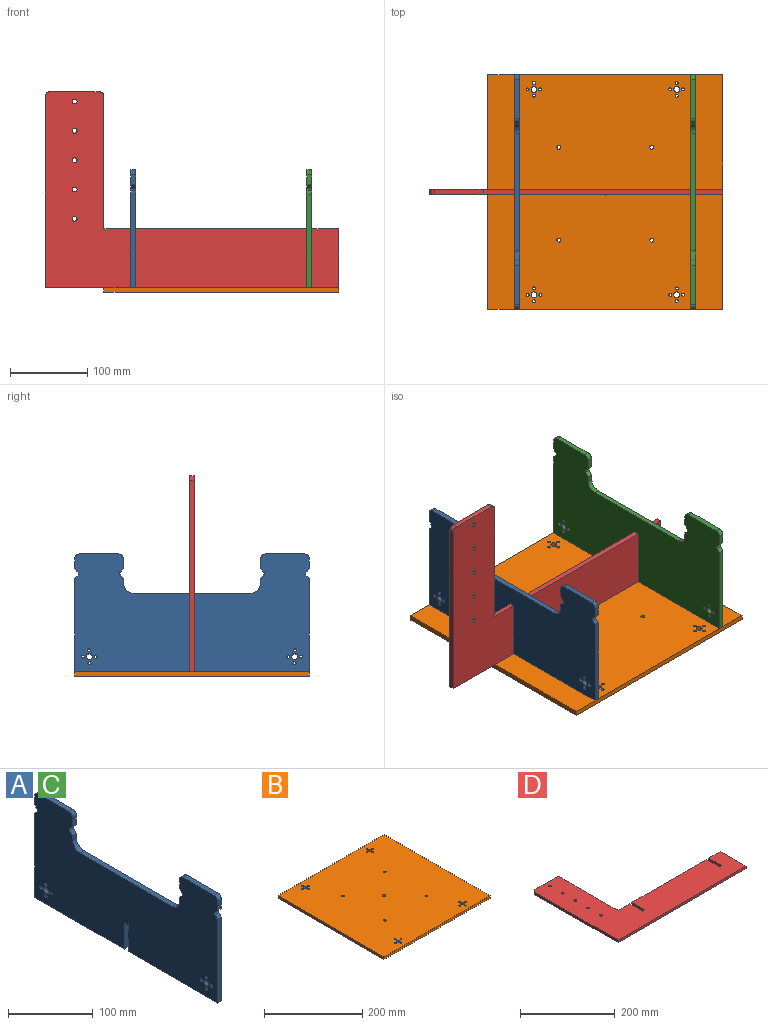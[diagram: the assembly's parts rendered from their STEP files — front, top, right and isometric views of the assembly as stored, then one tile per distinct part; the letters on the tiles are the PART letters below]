
ASSEMBLY  parts=4 mates=7
PART A: 46 faces, bbox 6.4x304.8x152.4 mm
  f0: plane 304.8x152.4mm, normal (1,0,0), area 36873.8mm2, adj f2,f3,f4,f5,f6,f7,f8,f9
  f1: plane 304.8x152.4mm, normal (-1,0,0), area 36873.8mm2, adj f2,f3,f4,f5,f6,f7,f8,f9
  f2: plane 149.23x6.35mm, normal (0,0,-1), area 947.6mm2, adj f0,f1,f4,f35
  f3: plane 149.23x6.35mm, normal (0,0,-1), area 947.6mm2, adj f0,f1,f32,f34
  f4: plane 120.65x6.35mm, normal (0,1,0), area 766.1mm2, adj f0,f1,f2,f5
  f5: plane 6.35x4.55mm, normal (0,0.71,0.71), area 40.9mm2, adj f0,f1,f4,f6
  f6: cylinder r=2.54mm len=6.35mm, axis (-1,0,0), area 25.3mm2, adj f0,f1,f5,f7
  f7: plane 6.35x4.55mm, normal (0,0.71,-0.71), area 40.9mm2, adj f0,f1,f6,f8
  f8: plane 12.7x6.35mm, normal (0,1,0), area 80.6mm2, adj f0,f1,f7,f9
  f9: cylinder r=6.35mm len=6.35mm, axis (-1,0,0), area 63.3mm2, adj f0,f1,f8,f10
  f10: plane 50.8x6.35mm, normal (0,0,1), area 322.6mm2, adj f0,f1,f9,f11
  f11: cylinder r=6.35mm len=6.35mm, axis (-1,0,0), area 63.3mm2, adj f0,f1,f10,f12
  f12: plane 12.7x6.35mm, normal (0,-1,0), area 80.6mm2, adj f0,f1,f11,f13
  f13: plane 6.35x4.55mm, normal (0,-0.71,-0.71), area 40.9mm2, adj f0,f1,f12,f14
  f14: cylinder r=2.54mm len=6.35mm, axis (-1,0,0), area 25.3mm2, adj f0,f1,f13,f15
  f15: plane 6.35x4.55mm, normal (0,-0.71,0.71), area 40.9mm2, adj f0,f1,f14,f16
  f16: plane 6.35x6.35mm, normal (0,-1,0), area 40.3mm2, adj f0,f1,f15,f17
  f17: cylinder r=12.7mm len=12.7mm, axis (-1,0,0), area 126.7mm2, adj f0,f1,f16,f18
  f18: plane 152.4x6.35mm, normal (0,0,1), area 967.7mm2, adj f0,f1,f17,f19
  f19: cylinder r=12.7mm len=12.7mm, axis (-1,0,0), area 126.7mm2, adj f0,f1,f18,f20
  f20: plane 6.35x6.35mm, normal (0,1,0), area 40.3mm2, adj f0,f1,f19,f21
  f21: plane 6.35x4.55mm, normal (0,0.71,0.71), area 40.9mm2, adj f0,f1,f20,f22
  f22: cylinder r=2.54mm len=6.35mm, axis (-1,0,0), area 25.3mm2, adj f0,f1,f21,f23
  f23: plane 6.35x4.55mm, normal (0,0.71,-0.71), area 40.9mm2, adj f0,f1,f22,f24
  f24: plane 12.7x6.35mm, normal (0,1,0), area 80.6mm2, adj f0,f1,f23,f25
  f25: cylinder r=6.35mm len=6.35mm, axis (-1,0,0), area 63.3mm2, adj f0,f1,f24,f26
  f26: plane 50.8x6.35mm, normal (0,0,1), area 322.6mm2, adj f0,f1,f25,f27
  f27: cylinder r=6.35mm len=6.35mm, axis (-1,0,0), area 63.3mm2, adj f0,f1,f26,f28
  f28: plane 12.7x6.35mm, normal (0,-1,0), area 80.6mm2, adj f0,f1,f27,f29
  f29: plane 6.35x4.55mm, normal (0,-0.71,-0.71), area 40.9mm2, adj f0,f1,f28,f30
  f30: cylinder r=2.54mm len=6.35mm, axis (-1,0,0), area 25.3mm2, adj f0,f1,f29,f31
  f31: plane 6.35x4.55mm, normal (0,-0.71,0.71), area 40.9mm2, adj f0,f1,f30,f32
  f32: plane 120.65x6.35mm, normal (0,-1,0), area 766.1mm2, adj f0,f1,f3,f31
  f33: plane 6.35x6.35mm, normal (0,0,-1), area 40.3mm2, adj f0,f1,f34,f35
  f34: plane 38.1x6.35mm, normal (0,1,0), area 241.9mm2, adj f0,f1,f3,f33
  f35: plane 38.1x6.35mm, normal (0,-1,0), area 241.9mm2, adj f0,f1,f2,f33
  f36: cylinder r=3.81mm len=7.62mm, axis (1,0,0), area 152mm2, adj f0,f1
  f37: cylinder r=1.91mm len=6.35mm, axis (1,0,0), area 76mm2, adj f0,f1
  f38: cylinder r=3.81mm len=7.62mm, axis (1,0,0), area 152mm2, adj f0,f1
  f39: cylinder r=1.91mm len=6.35mm, axis (1,0,0), area 76mm2, adj f0,f1
  f40: cylinder r=1.91mm len=6.35mm, axis (1,0,0), area 76mm2, adj f0,f1
  f41: cylinder r=1.91mm len=6.35mm, axis (1,0,0), area 76mm2, adj f0,f1
  f42: cylinder r=1.91mm len=6.35mm, axis (1,0,0), area 76mm2, adj f0,f1
  f43: cylinder r=1.91mm len=6.35mm, axis (1,0,0), area 76mm2, adj f0,f1
  f44: cylinder r=1.91mm len=6.35mm, axis (1,0,0), area 76mm2, adj f0,f1
  f45: cylinder r=1.91mm len=6.35mm, axis (1,0,0), area 76mm2, adj f0,f1
PART B: 31 faces, bbox 304.8x304.8x6.4 mm
  f0: plane 304.8x6.35mm, normal (-1,0,0), area 1935.5mm2, adj f1,f28,f29,f30
  f1: plane 304.8x6.35mm, normal (0,-1,0), area 1935.5mm2, adj f0,f2,f29,f30
  f2: plane 304.8x6.35mm, normal (1,0,0), area 1935.5mm2, adj f1,f28,f29,f30
  f3: cylinder r=3.81mm len=7.62mm, axis (0,0,-1), area 152mm2, adj f29,f30
  f4: cylinder r=3.81mm len=7.62mm, axis (0,0,-1), area 152mm2, adj f29,f30
  f5: cylinder r=3.81mm len=7.62mm, axis (0,0,-1), area 152mm2, adj f29,f30
  f6: cylinder r=3.81mm len=7.62mm, axis (0,0,-1), area 152mm2, adj f29,f30
  f7: cylinder r=3.81mm len=7.62mm, axis (0,0,-1), area 152mm2, adj f29,f30
  f8: cylinder r=1.91mm len=6.35mm, axis (0,0,-1), area 76mm2, adj f29,f30
  f9: cylinder r=1.91mm len=6.35mm, axis (0,0,-1), area 76mm2, adj f29,f30
  f10: cylinder r=1.91mm len=6.35mm, axis (0,0,-1), area 76mm2, adj f29,f30
  f11: cylinder r=1.91mm len=6.35mm, axis (0,0,-1), area 76mm2, adj f29,f30
  f12: cylinder r=1.91mm len=6.35mm, axis (0,0,-1), area 76mm2, adj f29,f30
  f13: cylinder r=1.91mm len=6.35mm, axis (0,0,-1), area 76mm2, adj f29,f30
  f14: cylinder r=1.91mm len=6.35mm, axis (0,0,-1), area 76mm2, adj f29,f30
  f15: cylinder r=1.91mm len=6.35mm, axis (0,0,-1), area 76mm2, adj f29,f30
  f16: cylinder r=1.91mm len=6.35mm, axis (0,0,-1), area 76mm2, adj f29,f30
  f17: cylinder r=1.91mm len=6.35mm, axis (0,0,-1), area 76mm2, adj f29,f30
  f18: cylinder r=1.91mm len=6.35mm, axis (0,0,-1), area 76mm2, adj f29,f30
  f19: cylinder r=1.91mm len=6.35mm, axis (0,0,-1), area 76mm2, adj f29,f30
  f20: cylinder r=1.91mm len=6.35mm, axis (0,0,-1), area 76mm2, adj f29,f30
  f21: cylinder r=1.91mm len=6.35mm, axis (0,0,-1), area 76mm2, adj f29,f30
  f22: cylinder r=1.91mm len=6.35mm, axis (0,0,-1), area 76mm2, adj f29,f30
  f23: cylinder r=1.91mm len=6.35mm, axis (0,0,-1), area 76mm2, adj f29,f30
  f24: cylinder r=2.54mm len=6.35mm, axis (0,0,-1), area 101.3mm2, adj f29,f30
  f25: cylinder r=2.54mm len=6.35mm, axis (0,0,-1), area 101.3mm2, adj f29,f30
  f26: cylinder r=2.54mm len=6.35mm, axis (0,0,-1), area 101.3mm2, adj f29,f30
  f27: cylinder r=2.54mm len=6.35mm, axis (0,0,-1), area 101.3mm2, adj f29,f30
  f28: plane 304.8x6.35mm, normal (0,1,0), area 1935.5mm2, adj f0,f2,f29,f30
  f29: plane 304.8x304.8mm, normal (0,0,1), area 92411.5mm2, adj f0,f1,f2,f3,f4,f5,f6,f7
  f30: plane 304.8x304.8mm, normal (0,0,-1), area 92411.5mm2, adj f0,f1,f2,f3,f4,f5,f6,f7
PART C: same geometry as A
PART D: 23 faces, bbox 381x254x6.4 mm
  f0: plane 247.65x6.35mm, normal (-1,0,0), area 1572.6mm2, adj f1,f15,f16,f17
  f1: plane 381x6.35mm, normal (0,-1,0), area 2419.3mm2, adj f0,f2,f16,f17
  f2: plane 76.2x6.35mm, normal (1,0,0), area 483.9mm2, adj f1,f3,f16,f17
  f3: plane 34.93x6.35mm, normal (0,1,0), area 221.8mm2, adj f2,f4,f16,f17
  f4: plane 38.1x6.35mm, normal (-1,0,0), area 241.9mm2, adj f3,f5,f16,f17
  f5: plane 6.35x6.35mm, normal (0,1,0), area 40.3mm2, adj f4,f6,f16,f17
  f6: plane 38.1x6.35mm, normal (1,0,0), area 241.9mm2, adj f5,f7,f16,f17
  f7: plane 222.25x6.35mm, normal (0,1,0), area 1411.3mm2, adj f6,f8,f16,f17
  f8: plane 38.1x6.35mm, normal (-1,0,0), area 241.9mm2, adj f7,f9,f16,f17
  f9: plane 6.35x6.35mm, normal (0,1,0), area 40.3mm2, adj f8,f10,f16,f17
  f10: plane 38.1x6.35mm, normal (1,0,0), area 241.9mm2, adj f9,f11,f16,f17
  f11: plane 34.93x6.35mm, normal (0,1,0), area 221.8mm2, adj f10,f12,f16,f17
  f12: plane 171.45x6.35mm, normal (1,0,0), area 1088.7mm2, adj f11,f13,f16,f17
  f13: cylinder r=6.35mm len=6.35mm, axis (0,0,-1), area 63.3mm2, adj f12,f14,f16,f17
  f14: plane 63.5x6.35mm, normal (0,1,0), area 403.2mm2, adj f13,f15,f16,f17
  f15: cylinder r=6.35mm len=6.35mm, axis (0,0,-1), area 63.3mm2, adj f0,f14,f16,f17
  f16: plane 381x254mm, normal (0,0,1), area 41921mm2, adj f0,f1,f2,f3,f4,f5,f6,f7
  f17: plane 381x254mm, normal (0,0,-1), area 41921mm2, adj f0,f1,f2,f3,f4,f5,f6,f7
  f18: cylinder r=3.17mm len=6.35mm, axis (0,0,1), area 126.7mm2, adj f16,f17
  f19: cylinder r=3.17mm len=6.35mm, axis (0,0,1), area 126.7mm2, adj f16,f17
  f20: cylinder r=3.17mm len=6.35mm, axis (0,0,1), area 126.7mm2, adj f16,f17
  f21: cylinder r=3.17mm len=6.35mm, axis (0,0,1), area 126.7mm2, adj f16,f17
  f22: cylinder r=3.17mm len=6.35mm, axis (0,0,1), area 126.7mm2, adj f16,f17
PLACE A t=(-356.84,110.36,152.14)mm
PLACE B t=(-391.76,415.16,37.84)mm
PLACE C t=(-128.24,110.36,152.14)mm
PLACE D rot(axis=(1,0,0),90deg) t=(-467.96,265.94,120.39)mm
MATE planar C.f3 <-> B.f27  axis (0,0,-1) through (-125.06,184.98,44.19)mm
MATE planar C.f32 <-> B.f1  axis (0,-1,0) through (-125.06,110.36,104.51)mm
MATE fastened A.f33 <-> D.f9  axis (0,0,-1) through (-353.66,262.76,82.29)mm
MATE planar B.f28 <-> A.f4  axis (0,1,0) through (-239.36,415.16,41.01)mm
MATE planar C.f4 <-> B.f28  axis (0,1,0) through (-125.06,415.16,104.51)mm
MATE planar B.f2 <-> D.f2  axis (1,0,0) through (-86.96,262.76,41.01)mm
MATE fastened D.f5 <-> C.f33  axis (0,0,1) through (-125.06,262.76,82.29)mm
